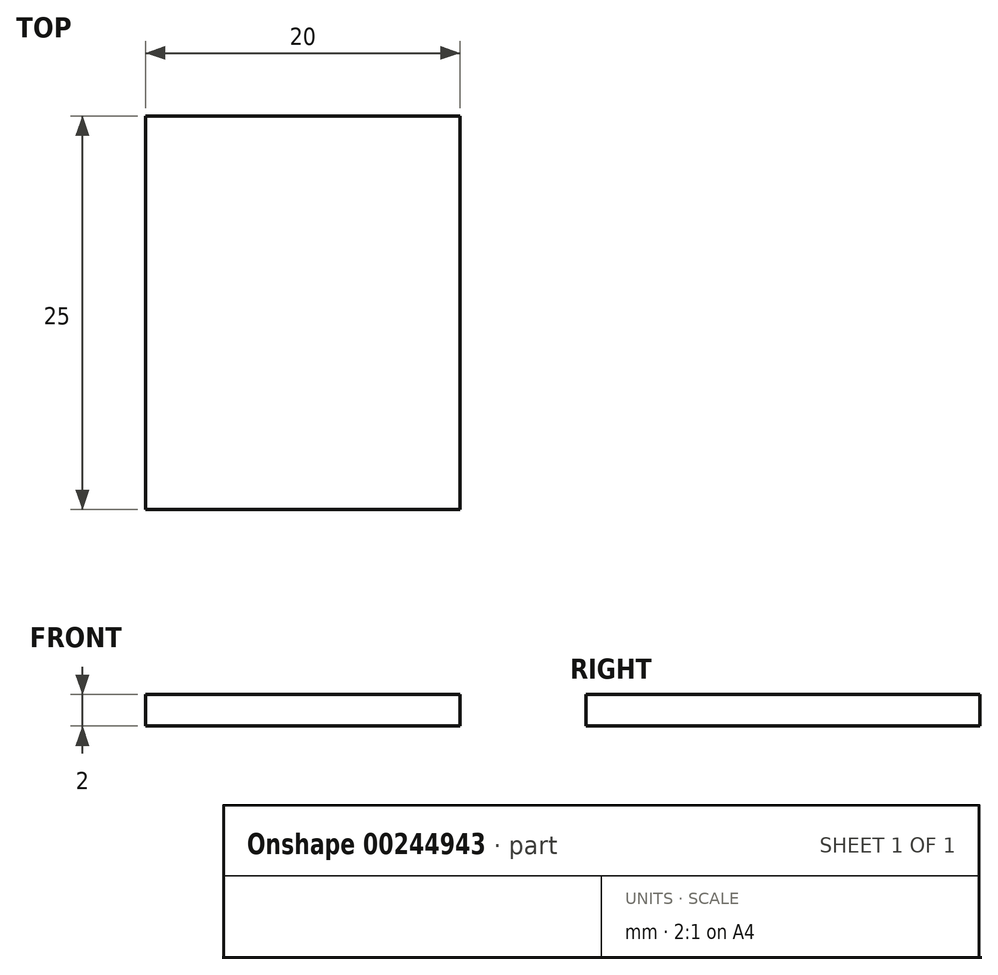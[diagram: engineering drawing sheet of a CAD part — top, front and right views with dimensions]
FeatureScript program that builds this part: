
annotation { "Feature Type Name" : "Feature", "Feature Type Description" : "" }
export const myFeature = defineFeature(function(context is Context, id is Id, definition is map)
    precondition{}
    {
        {
            var Q0;
            Q0=qCreatedBy(makeId("Top.planeOp"),FACE);
            var sketch = newSketch(context, id + "F0", { "sketchPlane" : qUnion([Q0])});
            skLineSegment(sketch, "E0.bottom", {"start": v(0, 0) * mm, "end": v(-20, 0) * mm});
            skLineSegment(sketch, "E0.top", {"start": v(0, 25) * mm, "end": v(-20, 25) * mm});
            skLineSegment(sketch, "E0.left", {"start": v(0, 0) * mm, "end": v(0, 25) * mm});
            skLineSegment(sketch, "E0.right", {"start": v(-20, 0) * mm, "end": v(-20, 25) * mm});
            skSolve(sketch);
        }
        {
            var Q0;
            Q0=makeQuery(id+"F0.imprint","IMPRINT",FACE,{"disambiguationData":[TD([[makeQuery(id+"F0.imprint","IMPRINT",EDGE,{"derivedFrom":sQuery(id+"F0.wireOp",EDGE,"E0.bottom")}),-1.0]])]});
            extrude(context, id + "F1", {"entities" : qUnion([Q0]), "depth" : 2 * mm, "offsetDistance" : 25 * mm});
        }
    });
